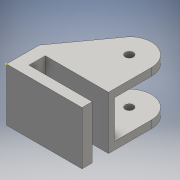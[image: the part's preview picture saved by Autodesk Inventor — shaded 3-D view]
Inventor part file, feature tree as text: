
AUTODESK INVENTOR PART (.ipt)
format: ipt  version: 2016 (Build 200138000, 138)  size: 122,368 bytes
history: native  units: mm
features: sketch x3, extrude x2
ambient origin geometry x8: Origin, YZ Plane, XZ Plane, XY Plane, X Axis, Y Axis, Z Axis, Center Point
bodies: Solid1 (feature_tree)
feature tree (5):
  extrude  "Extrusion1"  Depth=8.0mm
  sketch  "Sketch2"  dims[d7=20.0mm d8=4.0mm]
  extrude  "Extrusion2"  Depth=4.0mm
  sketch  "Sketch1"  dims[d3=8.0mm d6=18.0mm]
  sketch  "Sketch3"  dims[d9=3.0mm d10=5.0mm d11=16.0mm d12=37.004321mm d13=31.004321mm d14=26.173207mm d15=26.0mm d16=0.0mm d19=9.25mm d20=9.25mm d21=26.0mm d22=0.0mm]
